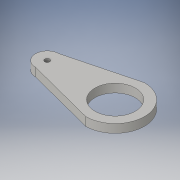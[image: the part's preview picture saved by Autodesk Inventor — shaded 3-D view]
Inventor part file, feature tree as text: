
AUTODESK INVENTOR PART (.ipt)
format: ipt  version: 2016 (Build 200138000, 138)  size: 103,424 bytes
history: native  units: in
note: dims shown in document units (in); Inventor stores cm internally (conversion verified against a paired STEP export)
features: extrude x1, sketch x1
ambient origin geometry x8: Origin, YZ Plane, XZ Plane, XY Plane, X Axis, Y Axis, Z Axis, Center Point
bodies: Solid1 (feature_tree)
feature tree (2):
  extrude  "Extrusion1"  Depth=0.18in
  sketch  "Sketch1"  dims[d0=0.86in d1=1.25in d2=1.445in d3=0.5in d4=0.105in d5=0.18in d6=0.0in]
